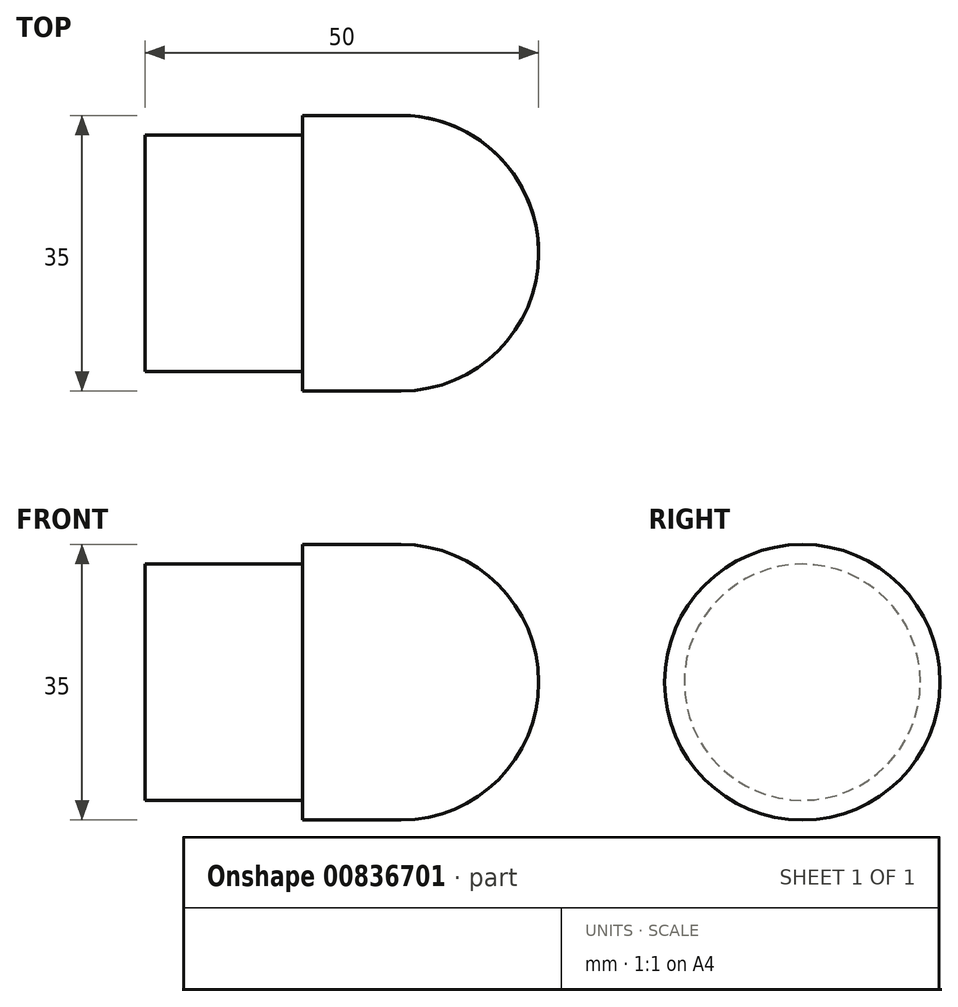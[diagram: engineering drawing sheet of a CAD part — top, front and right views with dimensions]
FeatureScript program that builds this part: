
annotation { "Feature Type Name" : "Feature", "Feature Type Description" : "" }
export const myFeature = defineFeature(function(context is Context, id is Id, definition is map)
    precondition{}
    {
        {
            var Q0;
            Q0=qCreatedBy(makeId("Top.planeOp"),FACE);
            var sketch = newSketch(context, id + "F0", { "sketchPlane" : qUnion([Q0])});
            skLineSegment(sketch, "E0", {"start": v(-25, 0) * mm, "end": v(-25, 15) * mm});
            skLineSegment(sketch, "E1", {"start": v(-25, 15) * mm, "end": v(-5, 15) * mm});
            skLineSegment(sketch, "E2", {"start": v(-5, 15) * mm, "end": v(-5, 17.5) * mm});
            skLineSegment(sketch, "E3", {"start": v(-5, 17.5) * mm, "end": v(7.5, 17.5) * mm});
            skLineSegment(sketch, "E4", {"start": v(-25, 0) * mm, "end": v(25, 0) * mm});
            skArc(sketch, "E5", {"start": v(7.5, 17.5) * mm, "mid": v(19.87, 12.37) * mm, "end": v(25, 0) * mm});
            skSolve(sketch);
        }
        {
            var Q0;
            Q0 = qSketchRegion(id + "F0", true);
            var Q1;
            Q1=sQuery(id+"F0.wireOp",EDGE,"E4");
            revolve(context, id + "F1", {"surfaceOperationType" : NewSurfaceOperationType.NEW, "entities" : qUnion([Q0]), "axis" : qUnion([Q1]), "revolveType" : RevolveType.FULL});
        }
    });
